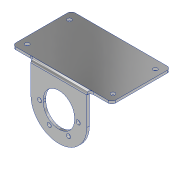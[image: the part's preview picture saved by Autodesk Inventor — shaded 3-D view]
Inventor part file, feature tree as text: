
AUTODESK INVENTOR PART (.ipt)
format: ipt  version: 2022 (Build 260153000, 153)  size: 222,720 bytes
history: native  units: mm
features: sketch x6, extrude x3, sheet_metal_op x2, hole x2, fillet x1, other x1, projected_geometry x1
ambient origin geometry x8: Origin, YZ Plane, XZ Plane, XY Plane, X Axis, Y Axis, Z Axis, Center Point
bodies: Solid1 (feature_tree)
feature tree (16):
  extrude  "Extrusion1"  Depth=6.5mm
  sheet_metal_op  "Face1"
  extrude  "Extrusion3"  Depth=45.0mm
  hole  "Hole1"  [1 undecoded]
  hole  "Hole2"  [1 undecoded]
  extrude  "Extrusion2"  Depth=2.0mm
  fillet  "Fillet2"  Radius=31.0mm
  sketch  "Sketch1"  dims[d1=37.0mm d3=6.5mm]
  sketch  "Sketch2"  dims[d4=50.0mm d5=45.0mm]
  other  "Plate1"
  sheet_metal_op  "Bend1"
  sketch  "Sketch3"  dims[d6=2.0mm d7=0.0mm d8=2.0mm]
  sketch  "Sketch4"  dims[d9=0.5mm d10=2.0mm d11=1.0mm]
  sketch  "Sketch6"  dims[d12=4.0mm d13=2.0mm d14=31.0mm]
  sketch  "Sketch8"  dims[d15=30.0mm d17=360.0deg d19=3.2mm d20=6.0mm d21=4.0mm d22=2.0mm d23=90.0deg d24=2.0mm d25=20.594885mm d26=34.0mm d27=69.0mm d28=3.2mm d29=6.0mm d30=4.0mm d31=2.0mm d32=90.0deg d33=8.0mm d34=20.594885mm d36=7.0mm d45=25.0mm d46=2.0mm d47=0.0mm d48=0.0mm d50=80.0mm d51=10.0mm d52=0.0mm d53=3.0mm]
  projected_geometry  "Project Cut Edges1"
note: 2 required parameter values undecoded (feature->parameter linkage not recoverable at this tier; creation-order binding heuristic only, values carry confidence <= 0.55)
